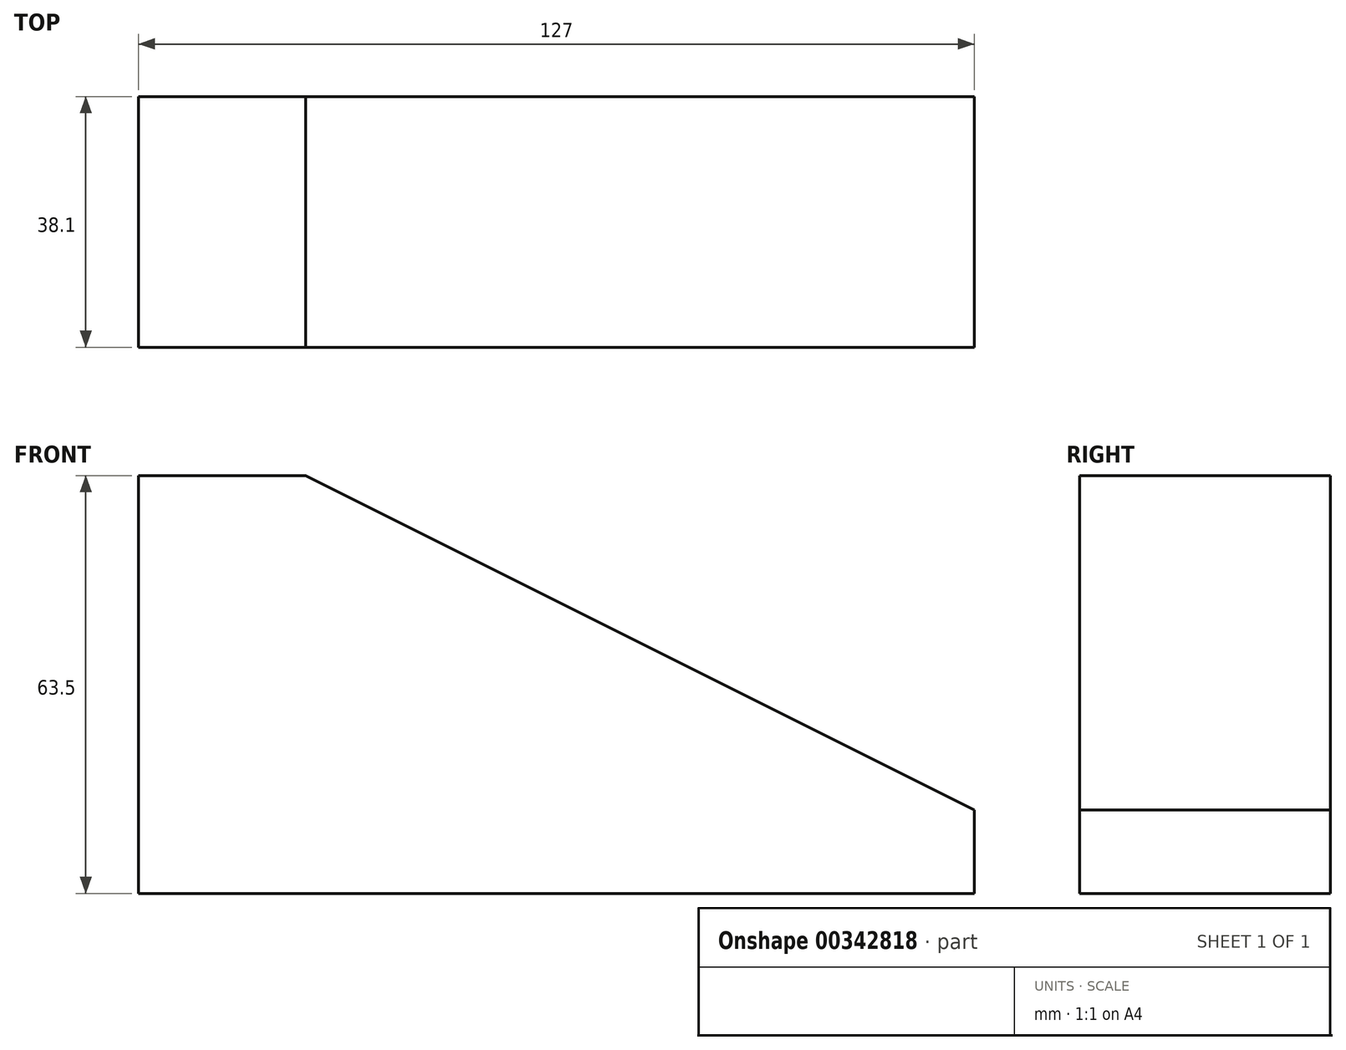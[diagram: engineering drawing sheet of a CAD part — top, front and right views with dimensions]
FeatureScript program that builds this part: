
annotation { "Feature Type Name" : "Feature", "Feature Type Description" : "" }
export const myFeature = defineFeature(function(context is Context, id is Id, definition is map)
    precondition{}
    {
        {
            var Q0;
            Q0=qCreatedBy(makeId("Front.planeOp"),FACE);
            var sketch = newSketch(context, id + "F0", { "sketchPlane" : qUnion([Q0])});
            skLineSegment(sketch, "E0", {"start": v(-45.2, 38.29) * mm, "end": v(-19.8, 38.29) * mm});
            skLineSegment(sketch, "E1", {"start": v(-45.2, 38.29) * mm, "end": v(-45.2, -25.21) * mm});
            skLineSegment(sketch, "E2", {"start": v(-45.2, -25.21) * mm, "end": v(81.8, -25.21) * mm});
            skLineSegment(sketch, "E3", {"start": v(81.8, -25.21) * mm, "end": v(81.8, -12.51) * mm});
            skLineSegment(sketch, "E4", {"start": v(-19.8, 38.29) * mm, "end": v(81.8, -12.51) * mm});
            skSolve(sketch);
        }
        {
            var Q0;
            Q0=makeQuery(id+"F0.imprint","IMPRINT",FACE,{"disambiguationData":[TD([[makeQuery(id+"F0.imprint","IMPRINT",EDGE,{"derivedFrom":sQuery(id+"F0.wireOp",EDGE,"E0")}),-1.0]])]});
            extrude(context, id + "F1", {"entities" : qUnion([Q0]), "depth" : 38.1 * mm});
        }
    });
